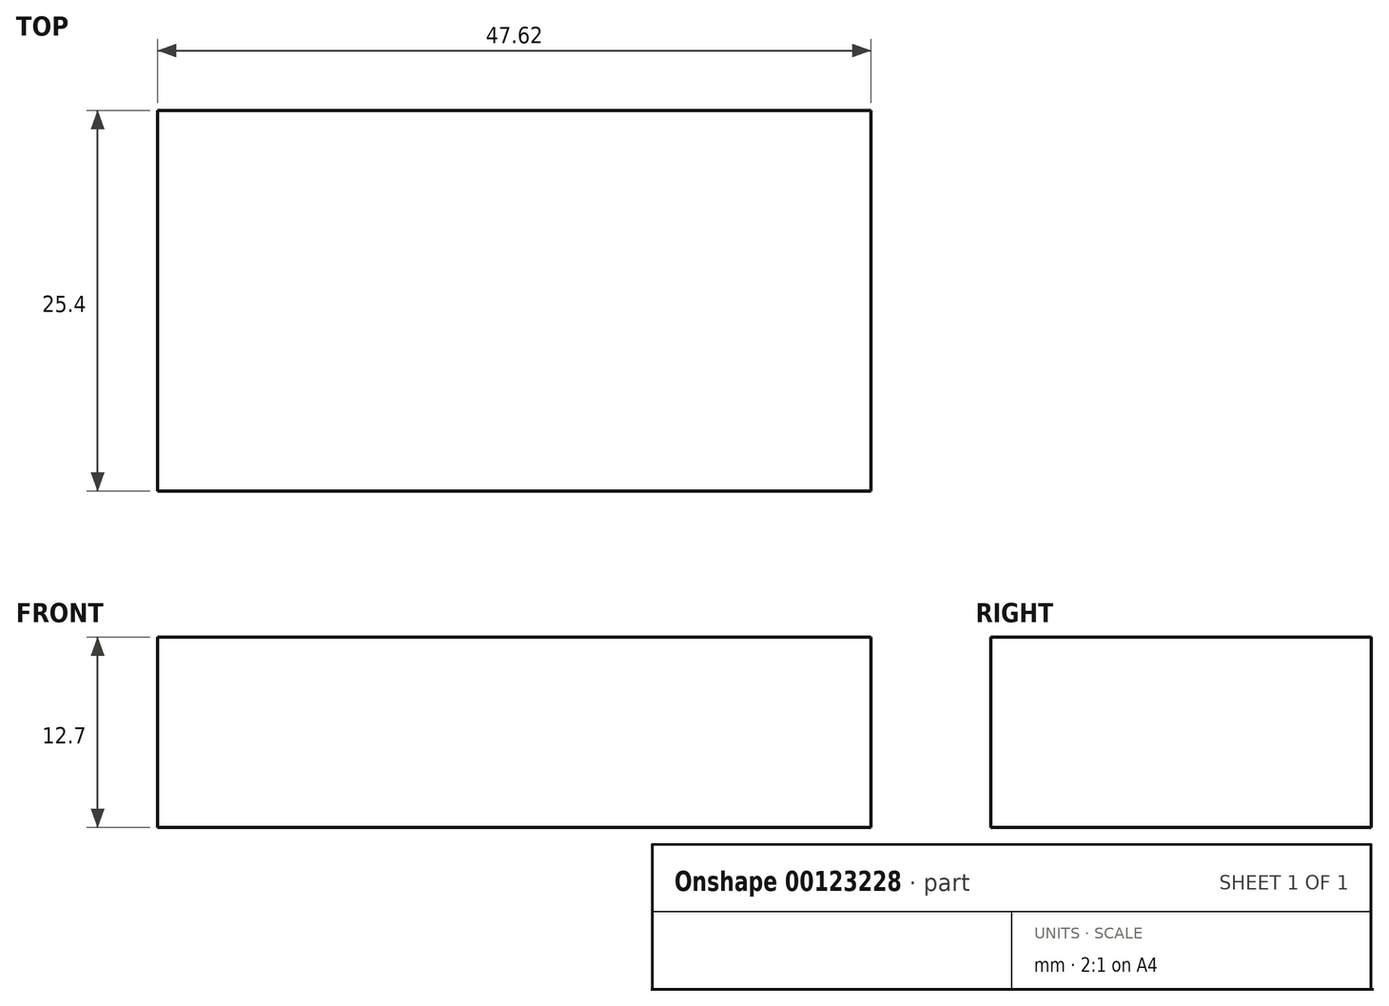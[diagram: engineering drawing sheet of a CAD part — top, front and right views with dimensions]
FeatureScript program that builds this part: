
annotation { "Feature Type Name" : "Feature", "Feature Type Description" : "" }
export const myFeature = defineFeature(function(context is Context, id is Id, definition is map)
    precondition{}
    {
        {
            var Q0;
            Q0=qCreatedBy(makeId("Top.planeOp"),FACE);
            var sketch = newSketch(context, id + "F0", { "sketchPlane" : qUnion([Q0])});
            skLineSegment(sketch, "E0.bottom", {"start": v(-17.75, 6.58) * mm, "end": v(29.87, 6.58) * mm});
            skLineSegment(sketch, "E0.top", {"start": v(-17.75, -18.82) * mm, "end": v(29.87, -18.82) * mm});
            skLineSegment(sketch, "E0.left", {"start": v(-17.75, 6.58) * mm, "end": v(-17.75, -18.82) * mm});
            skLineSegment(sketch, "E0.right", {"start": v(29.87, 6.58) * mm, "end": v(29.87, -18.82) * mm});
            skSolve(sketch);
        }
        {
            var Q0;
            Q0=makeQuery(id+"F0.imprint","IMPRINT",FACE,{"disambiguationData":[TD([[makeQuery(id+"F0.imprint","IMPRINT",EDGE,{"derivedFrom":sQuery(id+"F0.wireOp",EDGE,"E0.bottom")}),-1.0]])]});
            extrude(context, id + "F1", {"entities" : qUnion([Q0]), "depth" : 12.7 * mm});
        }
    });
